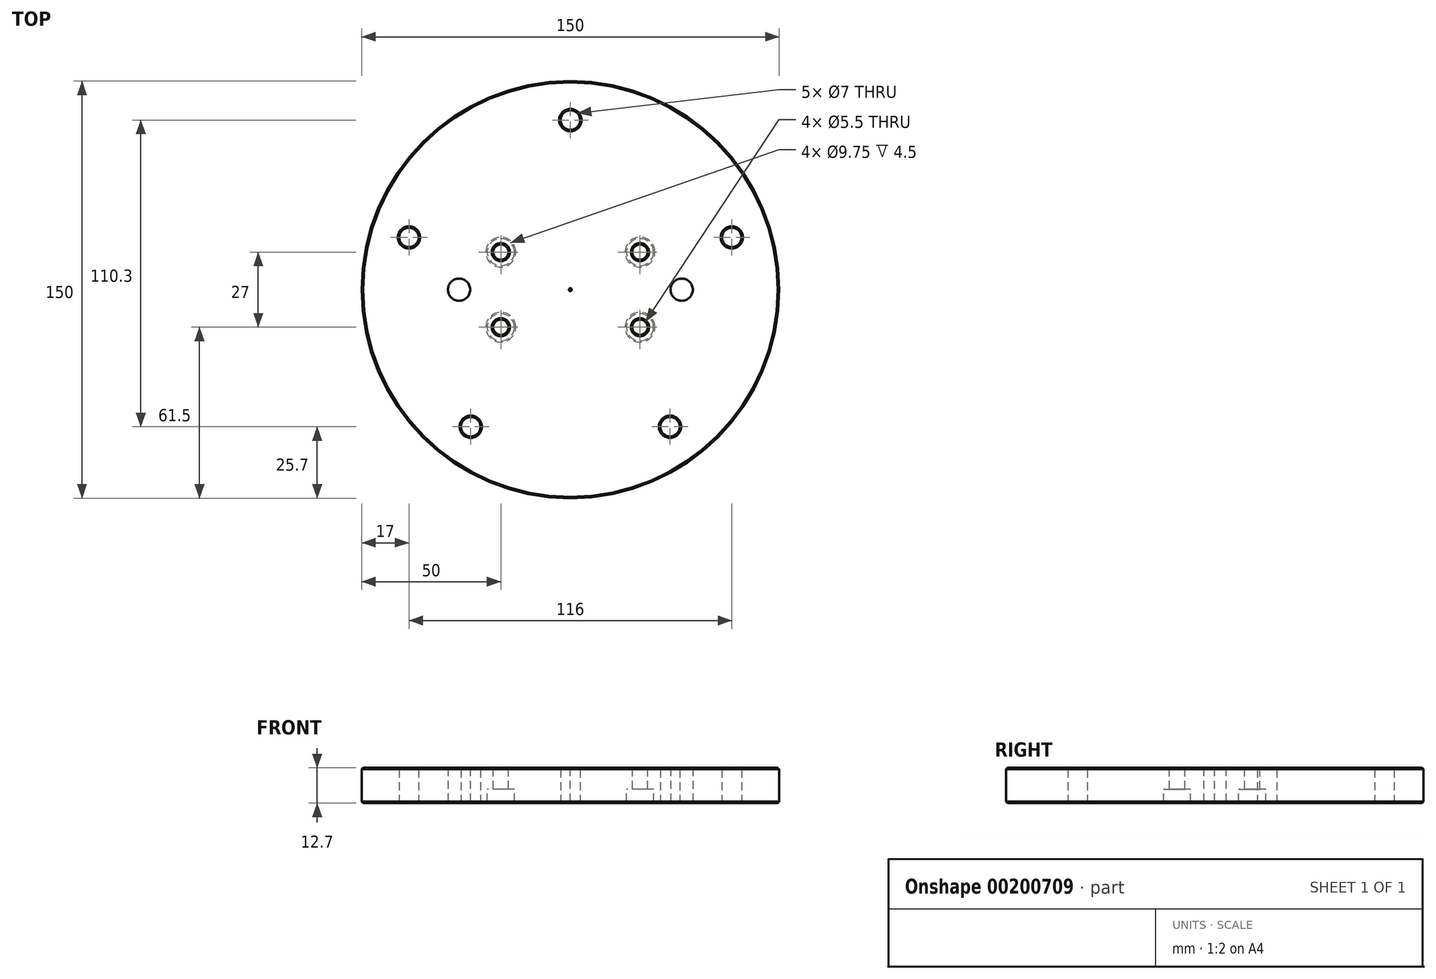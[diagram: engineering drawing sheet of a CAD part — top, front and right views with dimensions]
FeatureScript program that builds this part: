
annotation { "Feature Type Name" : "Feature", "Feature Type Description" : "" }
export const myFeature = defineFeature(function(context is Context, id is Id, definition is map)
    precondition{}
    {
        {
            var Q0;
            Q0=qCreatedBy(makeId("Top.planeOp"),FACE);
            var sketch = newSketch(context, id + "F0", { "sketchPlane" : qUnion([Q0])});
            skPoint(sketch, "E0.middle", {"position": v(0, 0) * mm});
            skCircle(sketch, "E1", {"center": v(0, 0) * mm, "radius": 75 * mm});
            skPoint(sketch, "E2", {"position": v(-25, 13.5) * mm});
            skPoint(sketch, "E3", {"position": v(25, 13.5) * mm});
            skPoint(sketch, "E4", {"position": v(25, -13.5) * mm});
            skPoint(sketch, "E5", {"position": v(-25, -13.5) * mm});
            skSolve(sketch);
        }
        {
            var Q0;
            Q0=makeQuery(id+"F0.imprint","IMPRINT",FACE,{"disambiguationData":[TD([[makeQuery(id+"F0.imprint","IMPRINT",EDGE,{"derivedFrom":sQuery(id+"F0.wireOp",EDGE,"E1")}),1.0]])]});
            extrude(context, id + "F1", {"entities" : qUnion([Q0]), "depth" : 12.7 * mm});
        }
        {
            var Q0;
            Q0=sQuery(id+"F0.wireOp",VERTEX,"E5");
            var Q1;
            Q1=sQuery(id+"F0.wireOp",VERTEX,"E4");
            var Q2;
            Q2=sQuery(id+"F0.wireOp",VERTEX,"E2");
            var Q3;
            Q3=sQuery(id+"F0.wireOp",VERTEX,"E3");
            var Q4;
            Q4=makeQuery(id+"F1.opExtrude","SWEPT_BODY",BODY,{"disambiguationData":[OSD([sQuery(id+"F0.wireOp",EDGE,"E1")])]});
            hole(context, id + "F2", {"style" : HoleStyle.C_BORE, "endStyle" : HoleEndStyle.THROUGH, "oppositeDirection" : true, "standardTappedOrClearance" : lookupTablePath({ "standard" : "ISO", "fit" : "Normal", "size" : "M5", "type" : "Clearance" }), "standardBlindInLast" : lookupTablePath({ "fit" : "Standard", "standard" : "ISO", "size" : "M5", "type" : "Clearance" }), "holeDiameter" : 5.5 * mm, "cBoreDiameter" : 9.75 * mm, "cBoreDepth" : 5 * mm, "locations" : qUnion([Q0, Q1, Q2, Q3]), "scope" : qUnion([Q4]), "tappedDepth" : 12 * mm, "tapClearance" : 3, "startStyle" : HoleStartStyle.SKETCH});
        }
        {
            var Q0;
            Q0=makeQuery(id+"F1.opExtrude","CAP_FACE",FACE,{"disambiguationData":[OSD([sQuery(id+"F0.wireOp",EDGE,"E1")])],"isStart":false});
            var sketch = newSketch(context, id + "F3", { "sketchPlane" : qUnion([Q0])});
            skPoint(sketch, "E6", {"position": v(0, 61) * mm});
            skPoint(sketch, "E7", {"position": v(-58, 18.8) * mm});
            skPoint(sketch, "E8", {"position": v(58, 18.8) * mm});
            skPoint(sketch, "E9", {"position": v(-35.8, -49.3) * mm});
            skPoint(sketch, "E10", {"position": v(35.8, -49.3) * mm});
            skSolve(sketch);
        }
        {
            var Q0;
            Q0=sQuery(id+"F3.wireOp",VERTEX,"E6");
            var Q1;
            Q1=sQuery(id+"F3.wireOp",VERTEX,"E8");
            var Q2;
            Q2=sQuery(id+"F3.wireOp",VERTEX,"E7");
            var Q3;
            Q3=sQuery(id+"F3.wireOp",VERTEX,"E9");
            var Q4;
            Q4=sQuery(id+"F3.wireOp",VERTEX,"E10");
            var Q5;
            Q5=makeQuery(id+"F1.opExtrude","SWEPT_BODY",BODY,{"disambiguationData":[OSD([sQuery(id+"F0.wireOp",EDGE,"E1")])]});
            hole(context, id + "F4", {"style" : HoleStyle.SIMPLE, "endStyle" : HoleEndStyle.THROUGH, "standardTappedOrClearance" : lookupTablePath({ "standard" : "ISO", "engagement" : "75%", "pitch" : "1 mm", "size" : "M8", "type" : "Tapped" }), "standardBlindInLast" : lookupTablePath({ "standard" : "ISO", "engagement" : "75%", "pitch" : "1 mm", "size" : "M8", "type" : "Tapped" }), "holeDiameter" : 7 * mm, "locations" : qUnion([Q0, Q1, Q2, Q3, Q4]), "scope" : qUnion([Q5]), "isTappedThrough" : true, "majorDiameter" : 8 * mm, "showTappedDepth" : true, "startStyle" : HoleStartStyle.SKETCH});
        }
        {
            var Q0;
            Q0=sQuery(id+"F0.wireOp",VERTEX,"E0.middle");
            var Q1;
            Q1=makeQuery(id+"F1.opExtrude","SWEPT_BODY",BODY,{"disambiguationData":[OSD([sQuery(id+"F0.wireOp",EDGE,"E1")])]});
            hole(context, id + "F5", {"style" : HoleStyle.SIMPLE, "endStyle" : HoleEndStyle.THROUGH, "oppositeDirection" : true, "standardTappedOrClearance" : lookupTablePath({ "standard" : "ANSI", "size" : "5/16 (0.31)", "type" : "Drilled" }), "standardBlindInLast" : lookupTablePath({ "standard" : "ANSI", "size" : "5/16", "type" : "Drilled" }), "holeDiameter" : 5 / 406.4 * mm, "locations" : qUnion([Q0]), "scope" : qUnion([Q1]), "isTappedThrough" : true, "startStyle" : HoleStartStyle.SKETCH});
        }
        {
            var Q0;
            Q0=makeQuery(id+"F1.opExtrude","CAP_FACE",FACE,{"disambiguationData":[OSD([sQuery(id+"F0.wireOp",EDGE,"E1")])],"isStart":true});
            var Q1;
            Q1=makeQuery(id+"F1.opExtrude","CAP_FACE",FACE,{"disambiguationData":[OSD([sQuery(id+"F0.wireOp",EDGE,"E1")])],"isStart":false});
            chamfer(context, id + "F6", {"entities" : qUnion([Q0, Q1]), "width" : .5 * mm, "tangentPropagation" : true});
        }
        {
            var Q0;
            Q0=makeQuery(id+"F1.opExtrude","CAP_FACE",FACE,{"disambiguationData":[OSD([sQuery(id+"F0.wireOp",EDGE,"E1")])],"isStart":false});
            var sketch = newSketch(context, id + "F7", { "sketchPlane" : qUnion([Q0])});
            skPoint(sketch, "E11.0", {"position": v(-25, 13.5) * mm});
            skPoint(sketch, "E12.0", {"position": v(25, 13.5) * mm});
            skPoint(sketch, "E13", {"position": v(-40, 0) * mm});
            skPoint(sketch, "E14", {"position": v(40, 0) * mm});
            skSolve(sketch);
        }
        {
            var Q0;
            Q0=sQuery(id+"F7.wireOp",VERTEX,"E13");
            var Q1;
            Q1=sQuery(id+"F7.wireOp",VERTEX,"E14");
            var Q2;
            Q2=makeQuery(id+"F1.opExtrude","SWEPT_BODY",BODY,{"disambiguationData":[OSD([sQuery(id+"F0.wireOp",EDGE,"E1")])]});
            hole(context, id + "F8", {"style" : HoleStyle.SIMPLE, "endStyle" : HoleEndStyle.THROUGH, "standardTappedOrClearance" : lookupTablePath({ "standard" : "ISO", "size" : "8", "type" : "Drilled" }), "standardBlindInLast" : lookupTablePath({ "standard" : "ISO", "size" : "8", "type" : "Drilled" }), "holeDiameter" : 8 * mm, "locations" : qUnion([Q0, Q1]), "scope" : qUnion([Q2]), "isTappedThrough" : true, "startStyle" : HoleStartStyle.SKETCH});
        }
    });
